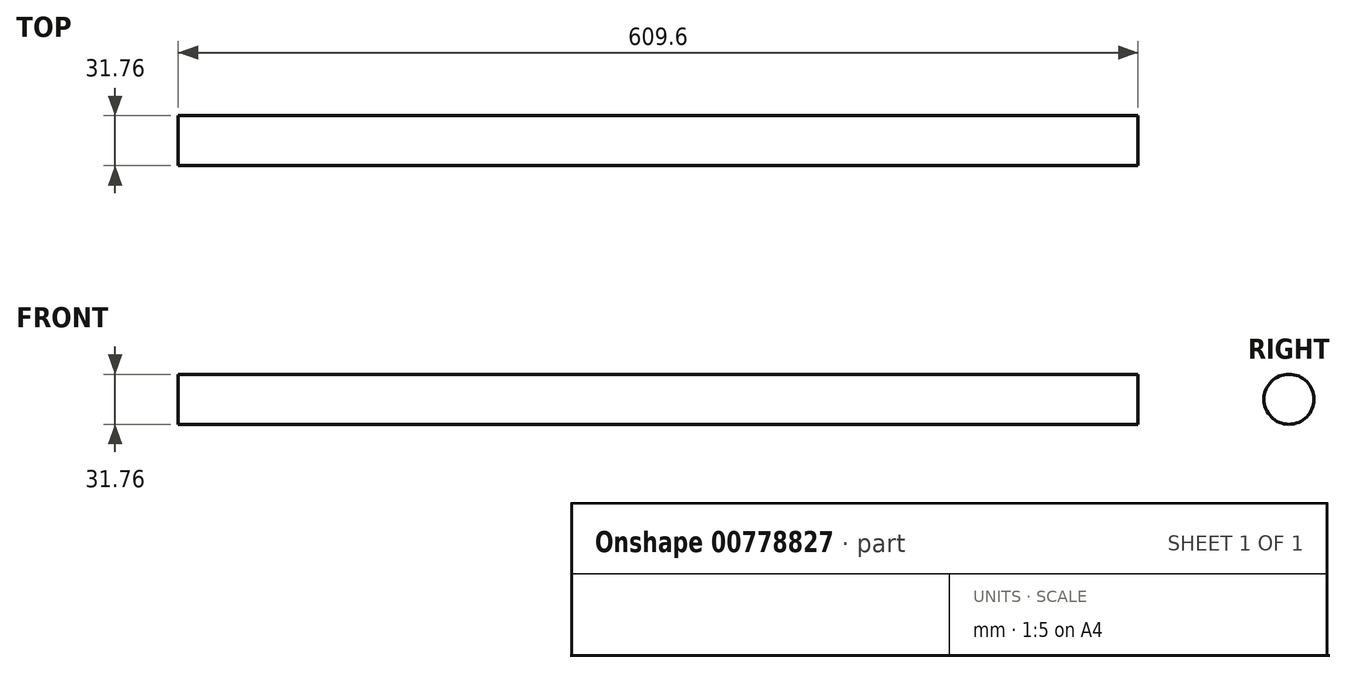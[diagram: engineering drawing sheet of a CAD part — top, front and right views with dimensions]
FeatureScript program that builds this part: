
annotation { "Feature Type Name" : "Feature", "Feature Type Description" : "" }
export const myFeature = defineFeature(function(context is Context, id is Id, definition is map)
    precondition{}
    {
        {
            var Q0;
            Q0=qCreatedBy(makeId("Right.planeOp"),FACE);
            var sketch = newSketch(context, id + "F0", { "sketchPlane" : qUnion([Q0])});
            skCircle(sketch, "E0", {"center": v(0, 0) * mm, "radius": 15.88 * mm});
            skSolve(sketch);
        }
        {
            var Q0;
            Q0 = qSketchRegion(id + "F0", true);
            extrude(context, id + "F1", {"entities" : qUnion([Q0]), "endBound" : BoundingType.SYMMETRIC, "depth" : 609.6 * mm, "offsetDistance" : 25.4 * mm});
        }
    });
